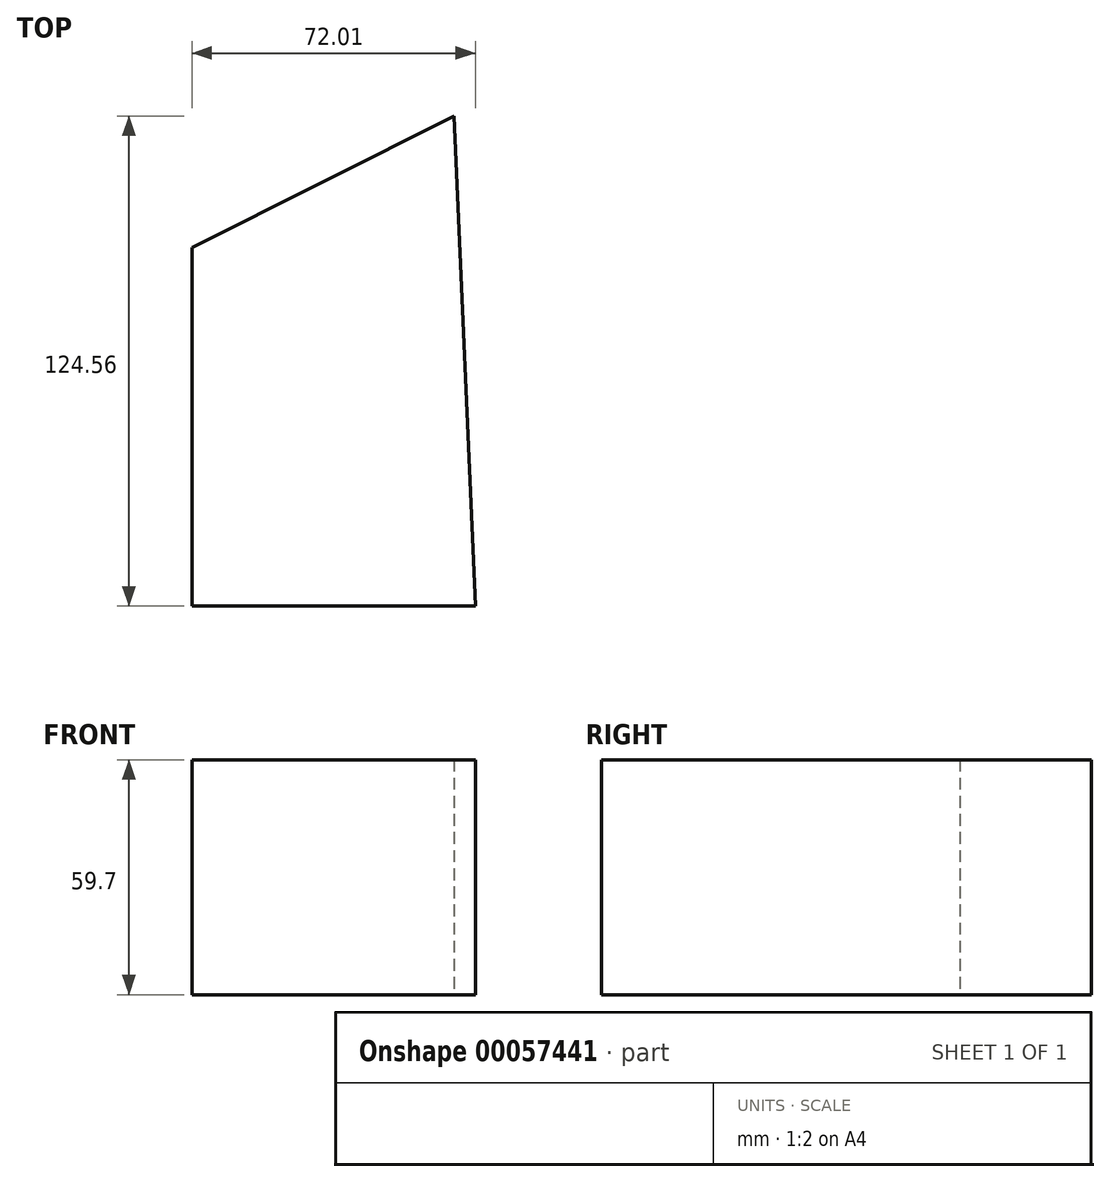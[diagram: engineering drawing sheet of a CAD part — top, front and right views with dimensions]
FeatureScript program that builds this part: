
annotation { "Feature Type Name" : "Feature", "Feature Type Description" : "" }
export const myFeature = defineFeature(function(context is Context, id is Id, definition is map)
    precondition{}
    {
        {
            var Q0;
            Q0=qCreatedBy(makeId("Top.planeOp"),FACE);
            var sketch = newSketch(context, id + "F0", { "sketchPlane" : qUnion([Q0])});
            skLineSegment(sketch, "E0", {"start": v(-109.67, 48.84) * mm, "end": v(-109.67, -42.26) * mm});
            skLineSegment(sketch, "E1", {"start": v(-109.67, -42.26) * mm, "end": v(-37.66, -42.26) * mm});
            skLineSegment(sketch, "E2", {"start": v(-37.66, -42.26) * mm, "end": v(-43.03, 82.3) * mm});
            skLineSegment(sketch, "E3", {"start": v(-43.03, 82.3) * mm, "end": v(-109.67, 48.84) * mm});
            skSolve(sketch);
        }
        {
            var Q0;
            Q0=makeQuery(id+"F0.imprint","IMPRINT",FACE,{"disambiguationData":[TD([[makeQuery(id+"F0.imprint","IMPRINT",EDGE,{"derivedFrom":sQuery(id+"F0.wireOp",EDGE,"E0")}),1.0]])]});
            extrude(context, id + "F1", {"entities" : qUnion([Q0]), "depth" : 59.7 * mm});
        }
    });
